# Revit family: Domotics-DomesticRanges-GEWISS-SYSTEM_DATA-TV_SOCKET
name_source: partatom
category: Apparecchi elettrici
revit_build: Autodesk Revit 2016 (Build: 20161004_0715(x64)
units: mm (PartAtom-declared; Revit-internal decimal feet)

## family parameters
Condiviso = Sì
Host = Superficie
Mantenere orientamento annotazione = Sì
Punto di calcolo locali = Sì
Quota connettore circolare = Usa diametro
Taglio con vuoti quando caricato = Sì
Tipo di parte = Normale

## types (8) — shared parameters
Carico apparente = 0 VA
Catalogue = DOMOTICS
Catalogue Range = SYSTEM - DOMESTIC RANGE
Description. = TV socket-outlet
Electrocod = 0131
For connector type = IEC-Male
Frequency = 5-2400 MHz
IDF = c0007aa7-9f71-4ec0-86c7-c021cd15d726
IDT = 554e1992-faed-42d9-9ef4-fadc3082a53c
Immagine tipo = GW21386.jpg
N. poli = 1
No. SYSTEM modules = 1
Produttore = GEWISS S.p.A.
Prospetto di default = 1219 mm
SEO = Socket outlet
Shielding = Class A
Technical sheet = https://www.gewiss.com
Tipo_ = SYSTEM PRESE TV_GENERICO : GW21386 Presa TV passante attenuata 5 dB conn. maschio 9,5mm nero
URL = https://www.gewiss.com
Version file RFA = 19.4
Volt = 230 V

## per-type parameters (varying)
| type | Attenuation | Colour | Description: | Descrizione | EAN code | Modello | Type |
| GW21381 - SOCKET-OUTLET TV DIR.C.M.9,5MM SY/BK | 0 dB | Black | Direct | SOCKET-OUTLET TV DIR.C.M.9,5MM SY/BK | 8011564128675 | GW21381 | With passage of current |
| GW21382 - THR.TV-SOCKET-10DB C.M.9,5MM SY/BK | 10 dB | Black | Feedtrough | THR.TV-SOCKET-10DB C.M.9,5MM SY/BK | 8011564128699 | GW21382 |  |
| GW21386 - THR.TV-SOCKET-5 DB C.M.9,5MM SY/BK | 5 dB | Black | Feedtrough | THR.TV-SOCKET-5 DB C.M.9,5MM SY/BK | 8011564128682 | GW21386 |  |
| GW20382 - THR.TV-SOCKET-10DB C.M.9,5MM SY/WT | 10 dB | White | Feedtrough | THR.TV-SOCKET-10DB C.M.9,5MM SY/WT | 8011564078888 | GW20382 |  |
| GW20386 - THR.TV-SOCKET-5 DB C.M.9,5MM SY/WT | 5 dB | White | Feedtrough | THR.TV-SOCKET-5 DB C.M.9,5MM SY/WT | 8011564078925 | GW20386 |  |
| GW20381 - SOCKET-OUTLET TV DIR.C.M.9,5MM SY/WT | 0 dB | White | Direct | SOCKET-OUTLET TV DIR.C.M.9,5MM SY/WT | 8011564078871 | GW20381 | With passage of current |
| GW21383 - THR.TV-SOCKET-14DB C.M.9,5MM SY/BK | 14 dB | Black | Feedtrough | THR.TV-SOCKET-14DB C.M.9,5MM SY/BK | 8011564128705 | GW21383 |  |
| GW20383 - THR.TV-SOCKET-14DB C.M.9,5MM SY/WT | 14 dB | White | Feedtrough | THR.TV-SOCKET-14DB C.M.9,5MM SY/WT | 8011564078895 | GW20383 |  |

## geometry (parser evidence)
native form markers: Sweep x2
no freeform markers — native parametric forms only
